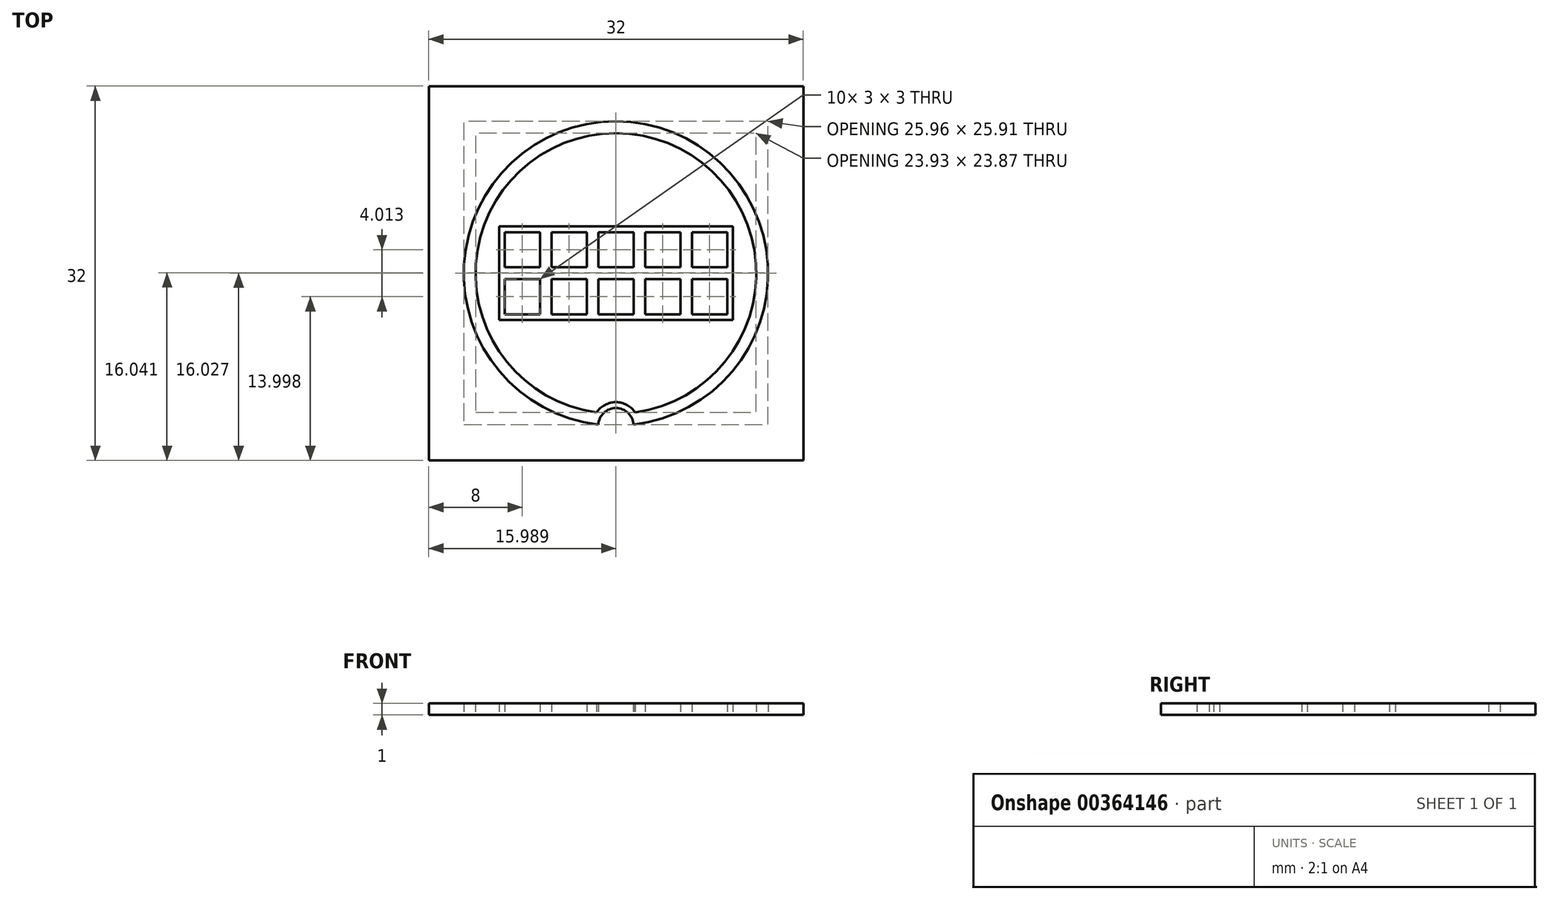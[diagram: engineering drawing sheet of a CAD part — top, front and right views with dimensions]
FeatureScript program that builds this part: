
annotation { "Feature Type Name" : "Feature", "Feature Type Description" : "" }
export const myFeature = defineFeature(function(context is Context, id is Id, definition is map)
    precondition{}
    {
        {
            var Q0;
            Q0=qCreatedBy(makeId("Top.planeOp"),FACE);
            var sketch = newSketch(context, id + "F0", { "sketchPlane" : qUnion([Q0])});
            skArc(sketch, "E0", {"start": v(1.64, -11.9) * mm, "mid": v(-0.01, 11.97) * mm, "end": v(-1.67, -11.9) * mm});
            skLineSegment(sketch, "E1", {"start": v(-0.01, -0.03) * mm, "end": v(0, -0.01) * mm});
            skArc(sketch, "E2", {"start": v(1.49, -12.94) * mm, "mid": v(-0.01, 12.97) * mm, "end": v(-1.5, -12.94) * mm});
            skArc(sketch, "E3", {"start": v(1.49, -12.94) * mm, "mid": v(-0.01, -11.53) * mm, "end": v(-1.5, -12.94) * mm});
            skArc(sketch, "E4", {"start": v(1.64, -11.9) * mm, "mid": v(-0.01, -11.03) * mm, "end": v(-1.67, -11.9) * mm});
            skLineSegment(sketch, "E5.bottom", {"start": v(16, -16.01) * mm, "end": v(-16, -16.01) * mm});
            skLineSegment(sketch, "E5.top", {"start": v(16, 15.99) * mm, "end": v(-16, 15.99) * mm});
            skLineSegment(sketch, "E5.left", {"start": v(16, -16.01) * mm, "end": v(16, 15.99) * mm});
            skLineSegment(sketch, "E5.right", {"start": v(-16, -16.01) * mm, "end": v(-16, 15.99) * mm});
            skPoint(sketch, "E5.middle", {"position": v(0, -0.01) * mm});
            skLineSegment(sketch, "E6.bottom", {"start": v(10, 4) * mm, "end": v(-10, 4) * mm});
            skLineSegment(sketch, "E6.top", {"start": v(10, -4) * mm, "end": v(-10, -4) * mm});
            skLineSegment(sketch, "E6.left", {"start": v(10, 4) * mm, "end": v(10, -4) * mm});
            skLineSegment(sketch, "E6.right", {"start": v(-10, 4) * mm, "end": v(-10, -4) * mm});
            skPoint(sketch, "E6.middle", {"position": v(0, 0) * mm});
            skLineSegment(sketch, "E7.bottom", {"start": v(-10, -4) * mm, "end": v(10, -4) * mm});
            skLineSegment(sketch, "E7.left", {"start": v(-10, -4) * mm, "end": v(-10, -0.01) * mm});
            skLineSegment(sketch, "E7.right", {"start": v(10, -4) * mm, "end": v(10, -0.01) * mm});
            skLineSegment(sketch, "E8.bottom", {"start": v(10, 4) * mm, "end": v(6, 4) * mm});
            skLineSegment(sketch, "E8.top", {"start": v(10, -4) * mm, "end": v(6, -4) * mm});
            skLineSegment(sketch, "E9.bottom", {"start": v(6, 4) * mm, "end": v(2, 4) * mm});
            skLineSegment(sketch, "E9.top", {"start": v(6, -4) * mm, "end": v(2, -4) * mm});
            skLineSegment(sketch, "E10.bottom", {"start": v(2, 4) * mm, "end": v(-2, 4) * mm});
            skLineSegment(sketch, "E10.top", {"start": v(2, -4) * mm, "end": v(-2, -4) * mm});
            skLineSegment(sketch, "E11.bottom", {"start": v(-2, 4) * mm, "end": v(-6, 4) * mm});
            skLineSegment(sketch, "E11.top", {"start": v(-2, -4) * mm, "end": v(-6, -4) * mm});
            skLineSegment(sketch, "E12.bottom", {"start": v(-10, 4) * mm, "end": v(-9.5, 4) * mm});
            skLineSegment(sketch, "E12.left", {"start": v(-10, 4) * mm, "end": v(-10, 3.5) * mm});
            skLineSegment(sketch, "E13.bottom", {"start": v(-9.5, 3.5) * mm, "end": v(-6.5, 3.5) * mm});
            skLineSegment(sketch, "E13.top", {"start": v(-9.5, 0.5) * mm, "end": v(-6.5, 0.5) * mm});
            skLineSegment(sketch, "E13.left", {"start": v(-9.5, 3.5) * mm, "end": v(-9.5, 0.5) * mm});
            skLineSegment(sketch, "E13.right", {"start": v(-6.5, 3.5) * mm, "end": v(-6.5, 0.5) * mm});
            skLineSegment(sketch, "E14.bottom", {"start": v(-6, 4) * mm, "end": v(-6.5, 4) * mm});
            skLineSegment(sketch, "E14.top", {"start": v(-6, -4) * mm, "end": v(-6.5, -4) * mm});
            skPoint(sketch, "E15.oppositeSnap0", {"position": v(-8, 3.5) * mm});
            skLineSegment(sketch, "E15.bottom", {"start": v(-10, 4) * mm, "end": v(10, 4) * mm});
            skLineSegment(sketch, "E15.right", {"start": v(10, 4) * mm, "end": v(10, 3.5) * mm});
            skLineSegment(sketch, "E16.top", {"start": v(-9.5, -0.51) * mm, "end": v(-6.5, -0.51) * mm});
            skLineSegment(sketch, "E16.left", {"start": v(-10, -0.01) * mm, "end": v(-10, -0.51) * mm});
            skLineSegment(sketch, "E16.right", {"start": v(10, -0.01) * mm, "end": v(10, -0.51) * mm});
            skLineSegment(sketch, "E17.bottom", {"start": v(-6.5, -0.51) * mm, "end": v(-9.5, -0.51) * mm});
            skLineSegment(sketch, "E17.top", {"start": v(-6.5, -3.51) * mm, "end": v(-9.5, -3.51) * mm});
            skLineSegment(sketch, "E17.left", {"start": v(-6.5, -0.51) * mm, "end": v(-6.5, -3.51) * mm});
            skLineSegment(sketch, "E17.right", {"start": v(-9.5, -0.51) * mm, "end": v(-9.5, -3.51) * mm});
            skLineSegment(sketch, "E18.trimOffspring", {"start": v(-5.5, -0.51) * mm, "end": v(-2.5, -0.51) * mm});
            skLineSegment(sketch, "E19.bottom", {"start": v(-6, 4) * mm, "end": v(-5.5, 4) * mm});
            skLineSegment(sketch, "E19.top", {"start": v(-6, -4) * mm, "end": v(-5.5, -4) * mm});
            skLineSegment(sketch, "E20.bottom", {"start": v(-5.5, 3.5) * mm, "end": v(-2.5, 3.5) * mm});
            skLineSegment(sketch, "E20.top", {"start": v(-5.5, 0.5) * mm, "end": v(-2.5, 0.5) * mm});
            skLineSegment(sketch, "E20.left", {"start": v(-5.5, 3.5) * mm, "end": v(-5.5, 0.5) * mm});
            skLineSegment(sketch, "E20.right", {"start": v(-2.5, 3.5) * mm, "end": v(-2.5, 0.5) * mm});
            skLineSegment(sketch, "E21.top", {"start": v(-5.5, -3.51) * mm, "end": v(-2.5, -3.51) * mm});
            skLineSegment(sketch, "E21.left", {"start": v(-5.5, -0.51) * mm, "end": v(-5.5, -3.51) * mm});
            skLineSegment(sketch, "E21.right", {"start": v(-2.5, -0.51) * mm, "end": v(-2.5, -3.51) * mm});
            skLineSegment(sketch, "E22.trimOffspring", {"start": v(-1.5, -0.51) * mm, "end": v(1.5, -0.51) * mm});
            skLineSegment(sketch, "E23.trimOffspring", {"start": v(-1.5, 3.5) * mm, "end": v(1.5, 3.5) * mm});
            skLineSegment(sketch, "E24.bottom", {"start": v(-2, 4) * mm, "end": v(-1.5, 4) * mm});
            skLineSegment(sketch, "E24.top", {"start": v(-2, -4) * mm, "end": v(-1.5, -4) * mm});
            skLineSegment(sketch, "E24.right", {"start": v(-1.5, 3.5) * mm, "end": v(-1.5, 0.5) * mm});
            skPoint(sketch, "E25.firstSnap0", {"position": v(-4, 3.5) * mm});
            skLineSegment(sketch, "E25.top", {"start": v(-1.5, 0.5) * mm, "end": v(1.5, 0.5) * mm});
            skLineSegment(sketch, "E25.right", {"start": v(1.5, 3.5) * mm, "end": v(1.5, 0.5) * mm});
            skLineSegment(sketch, "E26.top", {"start": v(-1.5, -3.51) * mm, "end": v(1.5, -3.51) * mm});
            skLineSegment(sketch, "E26.left", {"start": v(-1.5, -0.51) * mm, "end": v(-1.5, -3.51) * mm});
            skLineSegment(sketch, "E26.right", {"start": v(1.5, -0.51) * mm, "end": v(1.5, -3.51) * mm});
            skLineSegment(sketch, "E27.bottom", {"start": v(2, 4) * mm, "end": v(2.5, 4) * mm});
            skLineSegment(sketch, "E27.top", {"start": v(2, -4) * mm, "end": v(2.5, -4) * mm});
            skLineSegment(sketch, "E28.bottom", {"start": v(2.5, 3.5) * mm, "end": v(5.5, 3.5) * mm});
            skLineSegment(sketch, "E28.top", {"start": v(2.5, 0.5) * mm, "end": v(5.5, 0.5) * mm});
            skLineSegment(sketch, "E28.left", {"start": v(2.5, 3.5) * mm, "end": v(2.5, 0.5) * mm});
            skLineSegment(sketch, "E28.right", {"start": v(5.5, 3.5) * mm, "end": v(5.5, 0.5) * mm});
            skLineSegment(sketch, "E29.bottom", {"start": v(2.5, -0.51) * mm, "end": v(5.5, -0.51) * mm});
            skLineSegment(sketch, "E29.top", {"start": v(2.5, -3.51) * mm, "end": v(5.5, -3.51) * mm});
            skLineSegment(sketch, "E29.left", {"start": v(2.5, -0.51) * mm, "end": v(2.5, -3.51) * mm});
            skLineSegment(sketch, "E29.right", {"start": v(5.5, -0.51) * mm, "end": v(5.5, -3.51) * mm});
            skLineSegment(sketch, "E30.bottom", {"start": v(6, 4) * mm, "end": v(6.5, 4) * mm});
            skLineSegment(sketch, "E30.top", {"start": v(6, -4) * mm, "end": v(6.5, -4) * mm});
            skLineSegment(sketch, "E31.bottom", {"start": v(6.5, 3.5) * mm, "end": v(9.5, 3.5) * mm});
            skLineSegment(sketch, "E31.top", {"start": v(6.5, 0.5) * mm, "end": v(9.5, 0.5) * mm});
            skLineSegment(sketch, "E31.left", {"start": v(6.5, 3.5) * mm, "end": v(6.5, 0.5) * mm});
            skLineSegment(sketch, "E31.right", {"start": v(9.5, 3.5) * mm, "end": v(9.5, 0.5) * mm});
            skLineSegment(sketch, "E32.bottom", {"start": v(6.5, -0.51) * mm, "end": v(9.5, -0.51) * mm});
            skLineSegment(sketch, "E32.top", {"start": v(6.5, -3.51) * mm, "end": v(9.5, -3.51) * mm});
            skLineSegment(sketch, "E32.left", {"start": v(6.5, -0.51) * mm, "end": v(6.5, -3.51) * mm});
            skLineSegment(sketch, "E32.right", {"start": v(9.5, -0.51) * mm, "end": v(9.5, -3.51) * mm});
            skSolve(sketch);
        }
        {
            var Q0;
            Q0=makeQuery(id+"F0.imprint","IMPRINT",FACE,{"disambiguationData":[TD([[makeQuery(id+"F0.imprint","IMPRINT",EDGE,{"derivedFrom":sQuery(id+"F0.wireOp",EDGE,"E6.right")}),1.0]])]});
            var Q1;
            Q1=makeQuery(id+"F0.imprint","IMPRINT",FACE,{"disambiguationData":[TD([[makeQuery(id+"F0.imprint","IMPRINT",EDGE,{"derivedFrom":sQuery(id+"F0.wireOp",EDGE,"E0")}),-1.0]])]});
            extrude(context, id + "F1", {"entities" : qUnion([Q0, Q1]), "depth" : 1 * mm});
        }
        {
            var Q0;
            Q0=makeQuery(id+"F0.imprint","IMPRINT",FACE,{"disambiguationData":[TD([[makeQuery(id+"F0.imprint","IMPRINT",EDGE,{"derivedFrom":sQuery(id+"F0.wireOp",EDGE,"E2")}),-1.0]])]});
            extrude(context, id + "F2", {"entities" : qUnion([Q0]), "depth" : 1 * mm});
        }
    });
